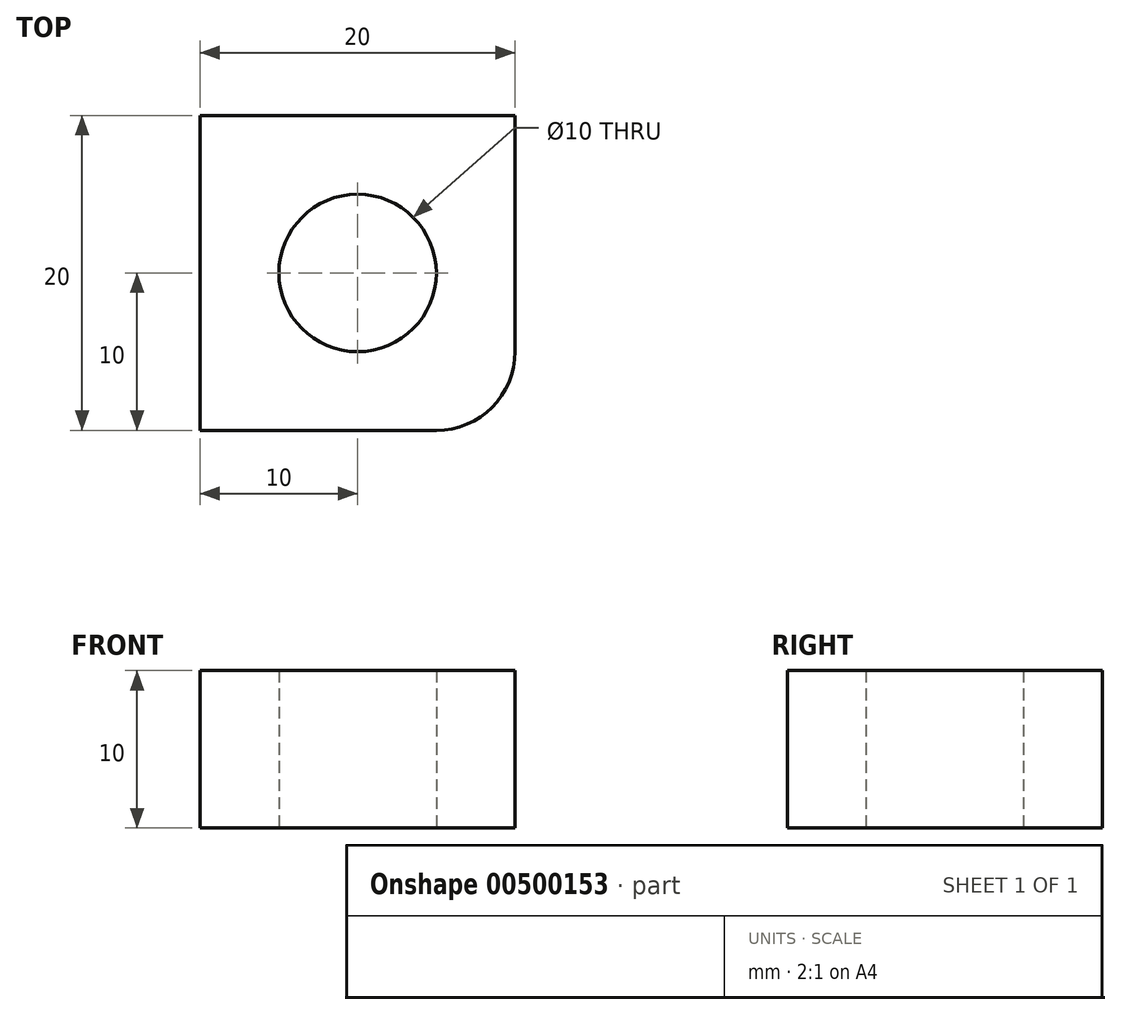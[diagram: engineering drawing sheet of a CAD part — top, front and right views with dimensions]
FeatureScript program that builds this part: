
annotation { "Feature Type Name" : "Feature", "Feature Type Description" : "" }
export const myFeature = defineFeature(function(context is Context, id is Id, definition is map)
    precondition{}
    {
        {
            var Q0;
            Q0=qCreatedBy(makeId("Top.planeOp"),FACE);
            var sketch = newSketch(context, id + "F0", { "sketchPlane" : qUnion([Q0])});
            skLineSegment(sketch, "E0", {"start": v(0, 0) * mm, "end": v(20, 0) * mm});
            skLineSegment(sketch, "E1", {"start": v(0, 0) * mm, "end": v(0, 20) * mm});
            skLineSegment(sketch, "E2", {"start": v(0, 20) * mm, "end": v(20, 20) * mm});
            skLineSegment(sketch, "E3", {"start": v(20, 20) * mm, "end": v(20, 0) * mm});
            skLineSegment(sketch, "E4", {"start": v(0, 0) * mm, "end": v(10, 0) * mm});
            skLineSegment(sketch, "E5", {"start": v(0, 0) * mm, "end": v(0, 10) * mm});
            skCircle(sketch, "E6", {"center": v(10, 10) * mm, "radius": 5 * mm});
            skSolve(sketch);
        }
        {
            var Q0;
            Q0=makeQuery(id+"F0.imprint","IMPRINT",FACE,{"disambiguationData":[TD([[makeQuery(id+"F0.imprint","IMPRINT",EDGE,{"derivedFrom":sQuery(id+"F0.wireOp",EDGE,"E0")}),1.0]])]});
            extrude(context, id + "F1", {"entities" : qUnion([Q0]), "depth" : 10 * mm});
        }
        {
            var Q0;
            Q0=makeQuery(id+"F1.opExtrude","SWEPT_EDGE",EDGE,{"disambiguationData":[OSD([sQuery(id+"F0.wireOp",EDGE,"E0"),sQuery(id+"F0.wireOp",EDGE,"E3")])]});
            fillet(context, id + "F2", {"entities" : qUnion([Q0]), "radius" : 5 * mm, "tangentPropagation" : true, "allowEdgeOverflow" : false});
        }
    });
